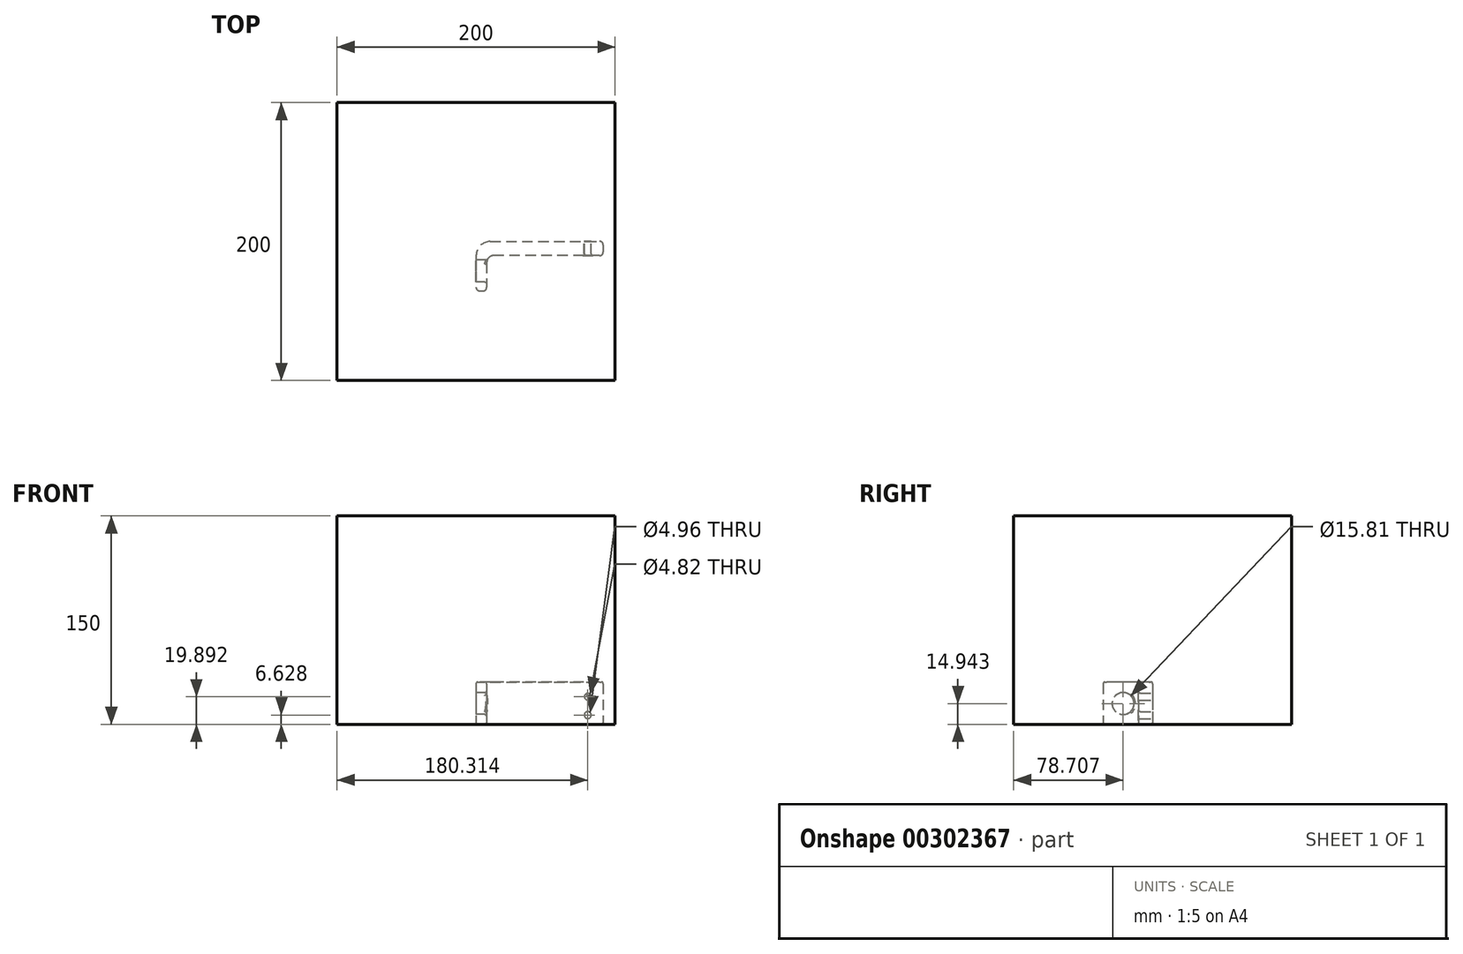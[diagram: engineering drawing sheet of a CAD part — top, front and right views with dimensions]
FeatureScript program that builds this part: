
annotation { "Feature Type Name" : "Feature", "Feature Type Description" : "" }
export const myFeature = defineFeature(function(context is Context, id is Id, definition is map)
    precondition{}
    {
        {
            var Q0;
            Q0=qCreatedBy(makeId("Top.planeOp"),FACE);
            var sketch = newSketch(context, id + "F0", { "sketchPlane" : qUnion([Q0])});
            skLineSegment(sketch, "E0.bottom", {"start": v(0, 0) * mm, "end": v(91.44, 0) * mm});
            skLineSegment(sketch, "E0.top", {"start": v(0, -35.56) * mm, "end": v(91.44, -35.56) * mm});
            skLineSegment(sketch, "E0.left", {"start": v(0, 0) * mm, "end": v(0, -35.56) * mm});
            skLineSegment(sketch, "E0.right", {"start": v(91.44, 0) * mm, "end": v(91.44, -35.56) * mm});
            skLineSegment(sketch, "E1", {"start": v(91.44, -10.16) * mm, "end": v(7.62, -10.16) * mm});
            skLineSegment(sketch, "E2", {"start": v(7.62, -10.16) * mm, "end": v(7.62, -35.56) * mm});
            skSolve(sketch);
        }
        {
            var Q0;
            {var subQ1=sQuery(id+"F0.wireOp",EDGE,"E0.bottom");Q0=makeQuery(id+"F0.imprint","IMPRINT",FACE,{"disambiguationData":[TD([[makeQuery(id+"F0.imprint","IMPRINT",EDGE,{"derivedFrom":subQ1}),-1.0]])]});}
            extrude(context, id + "F1", {"entities" : qUnion([Q0]), "depth" : 30.48 * mm});
        }
        {
            var Q0;
            Q0=makeQuery(id+"F1.opExtrude","SWEPT_EDGE",EDGE,{"disambiguationData":[OSD([sQuery(id+"F0.wireOp",EDGE,"E1"),sQuery(id+"F0.wireOp",EDGE,"E2")])]});
            fillet(context, id + "F2", {"entities" : qUnion([Q0]), "radius" : 5.08 * mm, "tangentPropagation" : true, "allowEdgeOverflow" : false});
        }
        {
            var Q0;
            Q0=makeQuery(id+"F1.opExtrude","SWEPT_EDGE",EDGE,{"disambiguationData":[OSD([sQuery(id+"F0.wireOp",EDGE,"E0.top"),sQuery(id+"F0.wireOp",EDGE,"E2")])]});
            var Q1;
            Q1=makeQuery(id+"F1.opExtrude","SWEPT_EDGE",EDGE,{"disambiguationData":[OSD([sQuery(id+"F0.wireOp",EDGE,"E0.right"),sQuery(id+"F0.wireOp",EDGE,"E1")])]});
            var Q2;
            Q2=makeQuery(id+"F1.opExtrude","SWEPT_EDGE",EDGE,{"disambiguationData":[OSD([sQuery(id+"F0.wireOp",EDGE,"E0.bottom"),sQuery(id+"F0.wireOp",EDGE,"E0.right")])]});
            var Q3;
            Q3=makeQuery(id+"F1.opExtrude","SWEPT_EDGE",EDGE,{"disambiguationData":[OSD([sQuery(id+"F0.wireOp",EDGE,"E0.top"),sQuery(id+"F0.wireOp",EDGE,"E0.left")])]});
            fillet(context, id + "F3", {"entities" : qUnion([Q0, Q1, Q2, Q3]), "radius" : 2.54 * mm, "tangentPropagation" : true, "allowEdgeOverflow" : false});
        }
        {
            var Q0;
            Q0=makeQuery(id+"F1.opExtrude","SWEPT_EDGE",EDGE,{"disambiguationData":[OSD([sQuery(id+"F0.wireOp",EDGE,"E0.bottom"),sQuery(id+"F0.wireOp",EDGE,"E0.left")])]});
            fillet(context, id + "F4", {"entities" : qUnion([Q0]), "radius" : 10.16 * mm, "tangentPropagation" : true, "allowEdgeOverflow" : false});
        }
        {
            var Q0;
            Q0=makeQuery(id+"F1.opExtrude","CAP_FACE",FACE,{"disambiguationData":[OSD([sQuery(id+"F0.wireOp",EDGE,"E0.bottom"),sQuery(id+"F0.wireOp",EDGE,"E0.top"),sQuery(id+"F0.wireOp",EDGE,"E0.left"),sQuery(id+"F0.wireOp",EDGE,"E0.right"),sQuery(id+"F0.wireOp",EDGE,"E1"),sQuery(id+"F0.wireOp",EDGE,"E2")])],"isStart":true});
            var Q1;
            Q1=makeQuery(id+"F1.opExtrude","CAP_FACE",FACE,{"disambiguationData":[OSD([sQuery(id+"F0.wireOp",EDGE,"E0.bottom"),sQuery(id+"F0.wireOp",EDGE,"E0.top"),sQuery(id+"F0.wireOp",EDGE,"E0.left"),sQuery(id+"F0.wireOp",EDGE,"E0.right"),sQuery(id+"F0.wireOp",EDGE,"E1"),sQuery(id+"F0.wireOp",EDGE,"E2")])],"isStart":false});
            fillet(context, id + "F5", {"entities" : qUnion([Q0, Q1]), "radius" : 1.27 * mm, "tangentPropagation" : true, "allowEdgeOverflow" : false});
        }
        {
            var Q0;
            Q0=makeQuery(id+"F1.opExtrude","SWEPT_FACE",FACE,{"disambiguationData":[OSD([sQuery(id+"F0.wireOp",EDGE,"E0.left")])]});
            var sketch = newSketch(context, id + "F6", { "sketchPlane" : qUnion([Q0])});
            skCircle(sketch, "E3", {"center": v(21.3, 14.94) * mm, "radius": 7.9 * mm});
            skSolve(sketch);
        }
        {
            var Q0;
            Q0 = qSketchRegion(id + "F6", true);
            extrude(context, id + "F7", {"entities" : qUnion([Q0]), "operationType" : NewBodyOperationType.REMOVE, "endBound" : BoundingType.THROUGH_ALL, "oppositeDirection" : true, "depth" : 25.4 * mm});
        }
        {
            var Q0;
            Q0=makeQuery(id+"F1.opExtrude","SWEPT_FACE",FACE,{"disambiguationData":[OSD([sQuery(id+"F0.wireOp",EDGE,"E0.bottom")])]});
            var sketch = newSketch(context, id + "F8", { "sketchPlane" : qUnion([Q0])});
            skCircle(sketch, "E4", {"center": v(-80.31, 19.9) * mm, "radius": 2.4 * mm});
            skCircle(sketch, "E5", {"center": v(-80.31, 6.63) * mm, "radius": 2.48 * mm});
            skSolve(sketch);
        }
        {
            var Q0;
            Q0 = qSketchRegion(id + "F8", true);
            extrude(context, id + "F9", {"entities" : qUnion([Q0]), "operationType" : NewBodyOperationType.REMOVE, "endBound" : BoundingType.THROUGH_ALL, "oppositeDirection" : true, "depth" : 25.4 * mm});
        }
        {
            var Q0;
            Q0=makeQuery(id+"F7.boolean.opBoolean","COPY",EDGE,{"derivedFrom":makeQuery(id+"F7.opExtrude","CAP_EDGE",EDGE,{"disambiguationData":[OSD([sQuery(id+"F6.wireOp",EDGE,"E3")])],"isStart":true})});
            var Q1;
            Q1=makeQuery(id+"F7.boolean.opBoolean","INTERSECT",EDGE,{"derivedFrom":[makeQuery(id+"F1.opExtrude","SWEPT_FACE",FACE,{"disambiguationData":[OSD([sQuery(id+"F0.wireOp",EDGE,"E2")])]}),makeQuery(id+"F7.opExtrude","SWEPT_FACE",FACE,{"disambiguationData":[OSD([sQuery(id+"F6.wireOp",EDGE,"E3")])]})]});
            var Q2;
            Q2=makeQuery(id+"F9.boolean.opBoolean","INTERSECT",EDGE,{"derivedFrom":[makeQuery(id+"F1.opExtrude","SWEPT_FACE",FACE,{"disambiguationData":[OSD([sQuery(id+"F0.wireOp",EDGE,"E1")])]}),makeQuery(id+"F9.opExtrude","SWEPT_FACE",FACE,{"disambiguationData":[OSD([sQuery(id+"F8.wireOp",EDGE,"E5")])]})]});
            var Q3;
            Q3=makeQuery(id+"F9.boolean.opBoolean","INTERSECT",EDGE,{"derivedFrom":[makeQuery(id+"F1.opExtrude","SWEPT_FACE",FACE,{"disambiguationData":[OSD([sQuery(id+"F0.wireOp",EDGE,"E1")])]}),makeQuery(id+"F9.opExtrude","SWEPT_FACE",FACE,{"disambiguationData":[OSD([sQuery(id+"F8.wireOp",EDGE,"E4")])]})]});
            var Q4;
            Q4=makeQuery(id+"F9.boolean.opBoolean","COPY",EDGE,{"derivedFrom":makeQuery(id+"F9.opExtrude","CAP_EDGE",EDGE,{"disambiguationData":[OSD([sQuery(id+"F8.wireOp",EDGE,"E4")])],"isStart":true})});
            var Q5;
            Q5=makeQuery(id+"F9.boolean.opBoolean","COPY",EDGE,{"derivedFrom":makeQuery(id+"F9.opExtrude","CAP_EDGE",EDGE,{"disambiguationData":[OSD([sQuery(id+"F8.wireOp",EDGE,"E5")])],"isStart":true})});
            fillet(context, id + "F10", {"entities" : qUnion([Q0, Q1, Q2, Q3, Q4, Q5]), "radius" : 1.27 * mm, "tangentPropagation" : true, "allowEdgeOverflow" : false});
        }
        {
            var Q0;
            Q0=qCreatedBy(makeId("Top.planeOp"),FACE);
            var sketch = newSketch(context, id + "F11", { "sketchPlane" : qUnion([Q0])});
            skLineSegment(sketch, "E6.bottom", {"start": v(100, -100) * mm, "end": v(-100, -100) * mm});
            skLineSegment(sketch, "E6.top", {"start": v(100, 100) * mm, "end": v(-100, 100) * mm});
            skLineSegment(sketch, "E6.left", {"start": v(100, -100) * mm, "end": v(100, 100) * mm});
            skLineSegment(sketch, "E6.right", {"start": v(-100, -100) * mm, "end": v(-100, 100) * mm});
            skPoint(sketch, "E6.middle", {"position": v(0, 0) * mm});
            skSolve(sketch);
        }
        {
            var Q0;
            Q0 = qSketchRegion(id + "F11", true);
            extrude(context, id + "F12", {"entities" : qUnion([Q0]), "depth" : 150 * mm, "offsetDistance" : 25 * mm});
        }
    });
